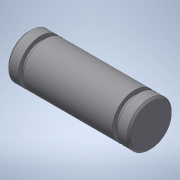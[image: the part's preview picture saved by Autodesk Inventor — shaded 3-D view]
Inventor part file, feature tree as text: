
AUTODESK INVENTOR PART (.ipt)
format: ipt  version: 2020 (Build 240168000, 168)  size: 154,112 bytes
history: native  units: in
note: dims shown in document units (in); Inventor stores cm internally (conversion verified against a paired STEP export)
features: other x49, revolve x1, sketch x1
ambient origin geometry x8: Origin, YZ Plane, XZ Plane, XY Plane, X Axis, Y Axis, Z Axis, Center Point
bodies: Solid1 (feature_tree)
feature tree (51):
  revolve  "Revolution1"  [1 undecoded]
  other  "p1_XY"
  other  "p1_YZ"
  other  "p1_ZX"
  other  "p1_X"
  other  "p1_Y"
  other  "p1_Z"
  other  "p1_Center"
  other  "p2_XY"
  other  "p2_YZ"
  other  "p2_ZX"
  other  "p2_X"
  other  "p2_Y"
  other  "p2_Z"
  other  "p2_Center"
  other  "pin_XY"
  other  "pin_YZ"
  other  "pin_ZX"
  other  "pin_X"
  other  "pin_Y"
  other  "pin_Z"
  other  "pin_Center"
  other  "rr1_XY"
  other  "rr1_YZ"
  other  "rr1_ZX"
  other  "rr1_X"
  other  "rr1_Y"
  other  "rr1_Z"
  other  "rr1_Center"
  other  "rr2_XY"
  other  "rr2_YZ"
  other  "rr2_ZX"
  other  "rr2_X"
  other  "rr2_Y"
  other  "rr2_Z"
  other  "rr2_Center"
  other  "w21_XY"
  other  "w21_YZ"
  other  "w21_ZX"
  other  "w21_X"
  other  "w21_Y"
  other  "w21_Z"
  other  "w21_Center"
  other  "w22_XY"
  other  "w22_YZ"
  other  "w22_ZX"
  other  "w22_X"
  other  "w22_Y"
  other  "w22_Z"
  other  "w22_Center"
  sketch  "Sketch_1"  dims[d0=360.0deg]
note: 1 required parameter value undecoded (feature->parameter linkage not recoverable at this tier; creation-order binding heuristic only, values carry confidence <= 0.55)
